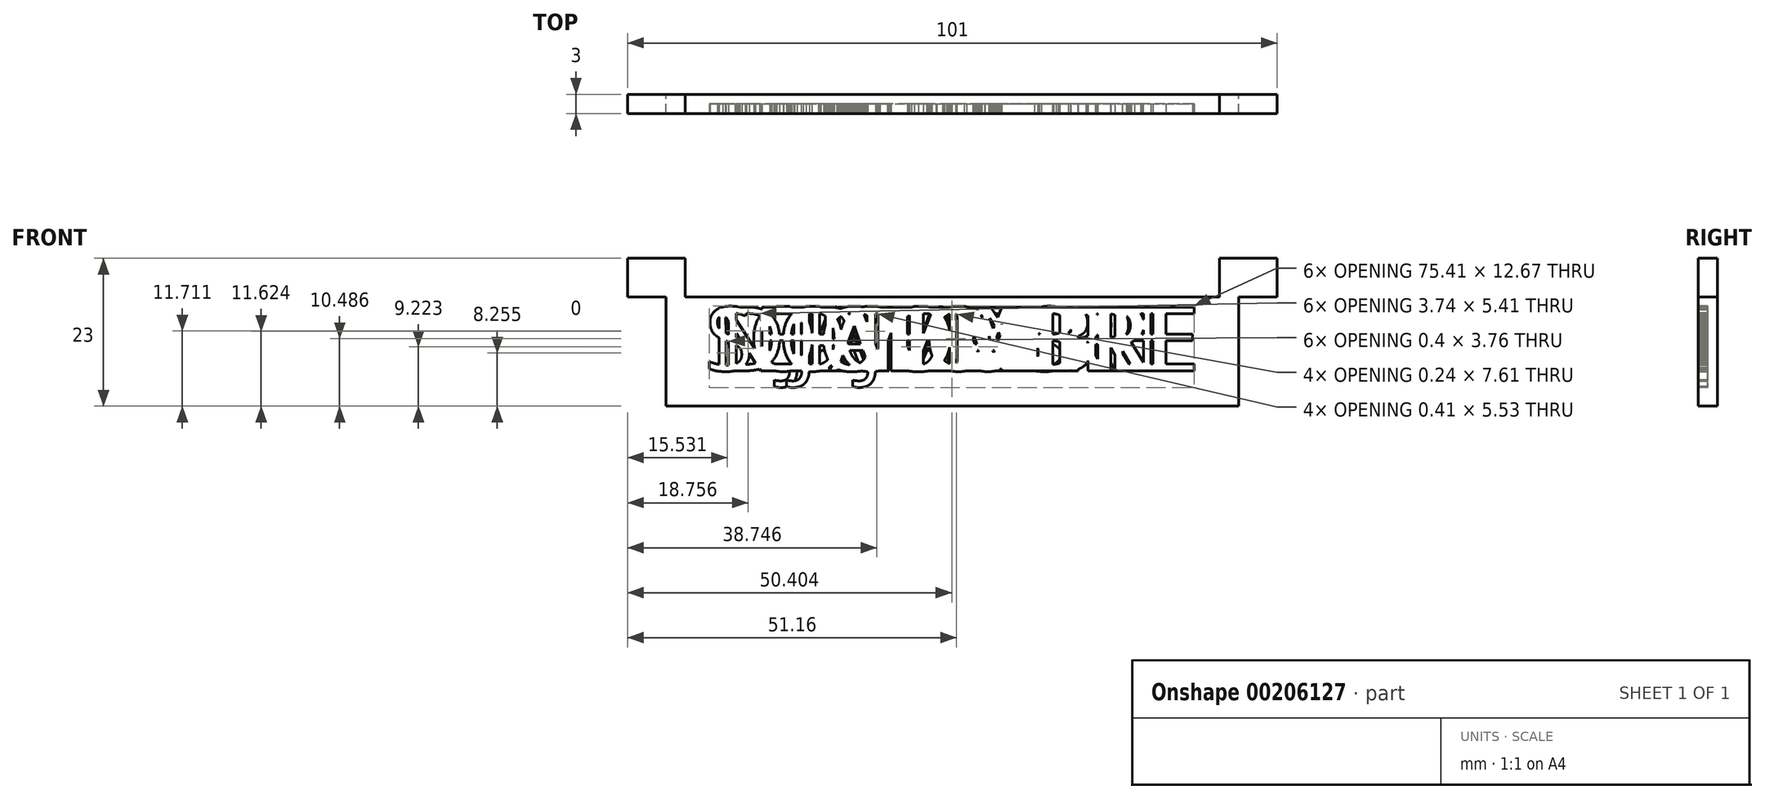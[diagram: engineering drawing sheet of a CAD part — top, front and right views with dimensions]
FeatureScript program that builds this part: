
annotation { "Feature Type Name" : "Feature", "Feature Type Description" : "" }
export const myFeature = defineFeature(function(context is Context, id is Id, definition is map)
    precondition{}
    {
        {
            var Q0;
            Q0=qCreatedBy(makeId("Front.planeOp"),FACE);
            var sketch = newSketch(context, id + "F0", { "sketchPlane" : qUnion([Q0])});
            skLineSegment(sketch, "E0.bottom", {"start": v(-51.5, 23) * mm, "end": v(-42.5, 23) * mm});
            skLineSegment(sketch, "E0.top", {"start": v(-45.5, 0) * mm, "end": v(43.5, 0) * mm});
            skLineSegment(sketch, "E0.left", {"start": v(-51.5, 23) * mm, "end": v(-51.5, 17) * mm});
            skLineSegment(sketch, "E0.right", {"start": v(49.5, 23) * mm, "end": v(49.5, 17) * mm});
            skLineSegment(sketch, "E1.top", {"start": v(-51.5, 17) * mm, "end": v(-45.5, 17) * mm});
            skLineSegment(sketch, "E1.right", {"start": v(-45.5, 0) * mm, "end": v(-45.5, 17) * mm});
            skLineSegment(sketch, "E2.bottom", {"start": v(-51.5, 23) * mm, "end": v(-42.5, 23) * mm, "construction": true});
            skLineSegment(sketch, "E2.top", {"start": v(-51.5, 17) * mm, "end": v(-42.5, 17) * mm, "construction": true});
            skLineSegment(sketch, "E2.left", {"start": v(-51.5, 23) * mm, "end": v(-51.5, 17) * mm, "construction": true});
            skLineSegment(sketch, "E2.right", {"start": v(-42.5, 23) * mm, "end": v(-42.5, 17) * mm, "construction": true});
            skLineSegment(sketch, "E3.top", {"start": v(-42.5, 17) * mm, "end": v(40.5, 17) * mm});
            skLineSegment(sketch, "E3.left", {"start": v(-42.5, 23) * mm, "end": v(-42.5, 17) * mm});
            skLineSegment(sketch, "E3.right", {"start": v(40.5, 23) * mm, "end": v(40.5, 17) * mm});
            skLineSegment(sketch, "E4.top", {"start": v(49.5, 17) * mm, "end": v(43.5, 17) * mm});
            skLineSegment(sketch, "E4.right", {"start": v(43.5, 0) * mm, "end": v(43.5, 17) * mm});
            skLineSegment(sketch, "E5.trimOffspring", {"start": v(40.5, 23) * mm, "end": v(49.5, 23) * mm});
            skSolve(sketch);
        }
        {
            var Q0;
            Q0=makeQuery(id+"F0.imprint","IMPRINT",FACE,{"disambiguationData":[TD([[makeQuery(id+"F0.imprint","IMPRINT",EDGE,{"derivedFrom":sQuery(id+"F0.wireOp",EDGE,"E0.bottom")}),-1.0]])]});
            extrude(context, id + "F1", {"entities" : qUnion([Q0]), "depth" : 3 * mm});
        }
        {
            var Q0;
            Q0=makeQuery(id+"F1.opExtrude","CAP_FACE",FACE,{"disambiguationData":[OSD([sQuery(id+"F0.wireOp",EDGE,"E0.bottom"),sQuery(id+"F0.wireOp",EDGE,"E0.top"),sQuery(id+"F0.wireOp",EDGE,"E0.left"),sQuery(id+"F0.wireOp",EDGE,"E0.right"),sQuery(id+"F0.wireOp",EDGE,"E1.top"),sQuery(id+"F0.wireOp",EDGE,"E1.right"),sQuery(id+"F0.wireOp",EDGE,"E3.top"),sQuery(id+"F0.wireOp",EDGE,"E3.left"),sQuery(id+"F0.wireOp",EDGE,"E3.right"),sQuery(id+"F0.wireOp",EDGE,"E4.top"),sQuery(id+"F0.wireOp",EDGE,"E4.right"),sQuery(id+"F0.wireOp",EDGE,"E5.trimOffspring")])],"isStart":false});
            var sketch = newSketch(context, id + "F2", { "sketchPlane" : qUnion([Q0])});
            skLineSegment(sketch, "E6.0", {"start": v(-45.5, 3.5) * mm, "end": v(-42, 3.5) * mm, "construction": true});
            skLineSegment(sketch, "E7.0", {"start": v(-42, 15.5) * mm, "end": v(40, 15.5) * mm, "construction": true});
            skLineSegment(sketch, "E8.0", {"start": v(-42, 0) * mm, "end": v(-42, 15.5) * mm, "construction": true});
            skText(sketch, "E9", { "text": "JANVIER", "fontName": "OpenSans-Regular.ttf"});
            skLineSegment(sketch, "E10.top", {"start": v(-45.5, 0) * mm, "end": v(-42, 0) * mm, "construction": true});
            skLineSegment(sketch, "E10.left", {"start": v(-45.5, 3.5) * mm, "end": v(-45.5, 0) * mm, "construction": true});
            skLineSegment(sketch, "E10.right", {"start": v(-42, 3.5) * mm, "end": v(-42, 0) * mm, "construction": true});
            skLineSegment(sketch, "E11.0", {"start": v(40, 0) * mm, "end": v(40, 17) * mm, "construction": true});
            skPoint(sketch, "E12.orphan", {"position": v(40, 15.5) * mm});
            skPoint(sketch, "E13.end.orphan", {"position": v(-1, 0) * mm});
            skLineSegment(sketch, "E14", {"start": v(-1, 17) * mm, "end": v(-1, 0) * mm, "construction": true});
            const initialGuessF2  = {"E9": [-0.02758, 0.0055, 1, 0, 0.01]};
            skSetInitialGuess(sketch, initialGuessF2);
            skSolve(sketch);
        }
        {
            var Q0;
            Q0=makeQuery(id+"F2.imprint","IMPRINT",FACE,{"disambiguationData":[TD([[makeQuery(id+"F2.imprint","IMPRINT",EDGE,{"derivedFrom":sQuery(id+"F2.wireOp",EDGE,"E9.sketch_text.stroke-0")}),-1.0]])]});
            var Q1;
            Q1=makeQuery(id+"F2.imprint","IMPRINT",FACE,{"disambiguationData":[TD([[makeQuery(id+"F2.imprint","IMPRINT",EDGE,{"derivedFrom":sQuery(id+"F2.wireOp",EDGE,"E9.sketch_text.stroke-10")}),-1.0]])]});
            var Q2;
            Q2=makeQuery(id+"F2.imprint","IMPRINT",FACE,{"disambiguationData":[TD([[makeQuery(id+"F2.imprint","IMPRINT",EDGE,{"derivedFrom":sQuery(id+"F2.wireOp",EDGE,"E9.sketch_text.stroke-23")}),-1.0]])]});
            var Q3;
            Q3=makeQuery(id+"F2.imprint","IMPRINT",FACE,{"disambiguationData":[TD([[makeQuery(id+"F2.imprint","IMPRINT",EDGE,{"derivedFrom":sQuery(id+"F2.wireOp",EDGE,"E9.sketch_text.stroke-38")}),-1.0]])]});
            var Q4;
            Q4=makeQuery(id+"F2.imprint","IMPRINT",FACE,{"disambiguationData":[TD([[makeQuery(id+"F2.imprint","IMPRINT",EDGE,{"derivedFrom":sQuery(id+"F2.wireOp",EDGE,"E9.sketch_text.stroke-52")}),-1.0]])]});
            var Q5;
            Q5=makeQuery(id+"F2.imprint","IMPRINT",FACE,{"disambiguationData":[TD([[makeQuery(id+"F2.imprint","IMPRINT",EDGE,{"derivedFrom":sQuery(id+"F2.wireOp",EDGE,"E9.sketch_text.stroke-65")}),-1.0]])]});
            var Q6;
            Q6=makeQuery(id+"F2.imprint","IMPRINT",FACE,{"disambiguationData":[TD([[makeQuery(id+"F2.imprint","IMPRINT",EDGE,{"derivedFrom":sQuery(id+"F2.wireOp",EDGE,"E9.sketch_text.stroke-47")}),-1.0]])]});
            extrude(context, id + "F3", {"entities" : qUnion([Q0, Q1, Q2, Q3, Q4, Q5, Q6]), "operationType" : NewBodyOperationType.REMOVE, "oppositeDirection" : true, "depth" : 1.5 * mm});
        }
        {
            var Q0;
            Q0=qSketchRegion(id+"F0",true);
            extrude(context, id + "F4", {"entities" : qUnion([Q0]), "depth" : 3 * mm});
        }
        {
            var Q0;
            Q0=makeQuery(id+"F4.opExtrude","CAP_FACE",FACE,{"disambiguationData":[OSD([sQuery(id+"F0.wireOp",EDGE,"E0.bottom"),sQuery(id+"F0.wireOp",EDGE,"E0.top"),sQuery(id+"F0.wireOp",EDGE,"E0.left"),sQuery(id+"F0.wireOp",EDGE,"E0.right"),sQuery(id+"F0.wireOp",EDGE,"E1.top"),sQuery(id+"F0.wireOp",EDGE,"E1.right"),sQuery(id+"F0.wireOp",EDGE,"E3.top"),sQuery(id+"F0.wireOp",EDGE,"E3.left"),sQuery(id+"F0.wireOp",EDGE,"E3.right"),sQuery(id+"F0.wireOp",EDGE,"E4.top"),sQuery(id+"F0.wireOp",EDGE,"E4.right"),sQuery(id+"F0.wireOp",EDGE,"E5.trimOffspring")])],"isStart":false});
            var sketch = newSketch(context, id + "F5", { "sketchPlane" : qUnion([Q0])});
            skText(sketch, "E15", { "text": "FEVRIER", "fontName": "OpenSans-Regular.ttf"});
            skPoint(sketch, "E16.orphan", {"position": v(36.68, 15.5) * mm});
            skPoint(sketch, "E17.end.orphan", {"position": v(-0.5, 0) * mm});
            skPoint(sketch, "E18.orphan", {"position": v(-38.68, 15.5) * mm});
            skLineSegment(sketch, "E19.0", {"start": v(-43.5, 15.5) * mm, "end": v(41.5, 15.5) * mm, "construction": true});
            skPoint(sketch, "E20.start.orphan", {"position": v(-1, 17) * mm});
            const initialGuessF5  = {"E15": [-0.0273, 0.0055, 1, 0, 0.01]};
            skSetInitialGuess(sketch, initialGuessF5);
            skSolve(sketch);
        }
        {
            var Q0;
            Q0=makeQuery(id+"F5.imprint","IMPRINT",FACE,{"disambiguationData":[TD([[makeQuery(id+"F5.imprint","IMPRINT",EDGE,{"derivedFrom":sQuery(id+"F5.wireOp",EDGE,"E15.sketch_text.stroke-0")}),-1.0]])]});
            var Q1;
            Q1=makeQuery(id+"F5.imprint","IMPRINT",FACE,{"disambiguationData":[TD([[makeQuery(id+"F5.imprint","IMPRINT",EDGE,{"derivedFrom":sQuery(id+"F5.wireOp",EDGE,"E15.sketch_text.stroke-10")}),-1.0]])]});
            var Q2;
            Q2=makeQuery(id+"F5.imprint","IMPRINT",FACE,{"disambiguationData":[TD([[makeQuery(id+"F5.imprint","IMPRINT",EDGE,{"derivedFrom":sQuery(id+"F5.wireOp",EDGE,"E15.sketch_text.stroke-22")}),-1.0]])]});
            var Q3;
            Q3=makeQuery(id+"F5.imprint","IMPRINT",FACE,{"disambiguationData":[TD([[makeQuery(id+"F5.imprint","IMPRINT",EDGE,{"derivedFrom":sQuery(id+"F5.wireOp",EDGE,"E15.sketch_text.stroke-47")}),-1.0]])]});
            var Q4;
            Q4=makeQuery(id+"F5.imprint","IMPRINT",FACE,{"disambiguationData":[TD([[makeQuery(id+"F5.imprint","IMPRINT",EDGE,{"derivedFrom":sQuery(id+"F5.wireOp",EDGE,"E15.sketch_text.stroke-65")}),-1.0]])]});
            var Q5;
            Q5=makeQuery(id+"F5.imprint","IMPRINT",FACE,{"disambiguationData":[TD([[makeQuery(id+"F5.imprint","IMPRINT",EDGE,{"derivedFrom":sQuery(id+"F5.wireOp",EDGE,"E15.sketch_text.stroke-79")}),-1.0]])]});
            var Q6;
            Q6=makeQuery(id+"F5.imprint","IMPRINT",FACE,{"disambiguationData":[TD([[makeQuery(id+"F5.imprint","IMPRINT",EDGE,{"derivedFrom":sQuery(id+"F5.wireOp",EDGE,"E15.sketch_text.stroke-49")}),-1.0]])]});
            var Q7;
            Q7=makeQuery(id+"F5.imprint","IMPRINT",FACE,{"disambiguationData":[TD([[makeQuery(id+"F5.imprint","IMPRINT",EDGE,{"derivedFrom":sQuery(id+"F5.wireOp",EDGE,"E15.sketch_text.stroke-53")}),-1.0]])]});
            extrude(context, id + "F6", {"entities" : qUnion([Q0, Q1, Q2, Q3, Q4, Q5, Q6, Q7]), "operationType" : NewBodyOperationType.REMOVE, "oppositeDirection" : true, "depth" : 1.5 * mm});
        }
        {
            var Q0;
            Q0=makeQuery(id+"F0.imprint","IMPRINT",FACE,{"disambiguationData":[TD([[makeQuery(id+"F0.imprint","IMPRINT",EDGE,{"derivedFrom":sQuery(id+"F0.wireOp",EDGE,"E0.bottom")}),-1.0]])]});
            extrude(context, id + "F7", {"entities" : qUnion([Q0]), "depth" : 3 * mm});
        }
        {
            var Q0;
            Q0=makeQuery(id+"F7.opExtrude","CAP_FACE",FACE,{"disambiguationData":[OSD([sQuery(id+"F0.wireOp",EDGE,"E0.bottom"),sQuery(id+"F0.wireOp",EDGE,"E0.top"),sQuery(id+"F0.wireOp",EDGE,"E0.left"),sQuery(id+"F0.wireOp",EDGE,"E0.right"),sQuery(id+"F0.wireOp",EDGE,"E1.top"),sQuery(id+"F0.wireOp",EDGE,"E1.right"),sQuery(id+"F0.wireOp",EDGE,"E3.top"),sQuery(id+"F0.wireOp",EDGE,"E3.left"),sQuery(id+"F0.wireOp",EDGE,"E3.right"),sQuery(id+"F0.wireOp",EDGE,"E4.top"),sQuery(id+"F0.wireOp",EDGE,"E4.right"),sQuery(id+"F0.wireOp",EDGE,"E5.trimOffspring")])],"isStart":false});
            var sketch = newSketch(context, id + "F8", { "sketchPlane" : qUnion([Q0])});
            skText(sketch, "E21", { "text": "MARS", "fontName": "OpenSans-Regular.ttf"});
            skPoint(sketch, "E22.orphan", {"position": v(29.28, 15.5) * mm});
            skPoint(sketch, "E23.end.orphan", {"position": v(0, -12.7) * mm});
            skPoint(sketch, "E24.orphan", {"position": v(-31.28, 15.5) * mm});
            skPoint(sketch, "E25.start.orphan", {"position": v(0, 4.3) * mm});
            skLineSegment(sketch, "E26.0", {"start": v(-43.5, 15.5) * mm, "end": v(41.5, 15.5) * mm, "construction": true});
            const initialGuessF8  = {"E21": [-0.01989, 0.0055, 1, 0, 0.01]};
            skSetInitialGuess(sketch, initialGuessF8);
            skSolve(sketch);
        }
        {
            var Q0;
            Q0=makeQuery(id+"F8.imprint","IMPRINT",FACE,{"disambiguationData":[TD([[makeQuery(id+"F8.imprint","IMPRINT",EDGE,{"derivedFrom":sQuery(id+"F8.wireOp",EDGE,"E21.sketch_text.stroke-0")}),-1.0]])]});
            var Q1;
            Q1=makeQuery(id+"F8.imprint","IMPRINT",FACE,{"disambiguationData":[TD([[makeQuery(id+"F8.imprint","IMPRINT",EDGE,{"derivedFrom":sQuery(id+"F8.wireOp",EDGE,"E21.sketch_text.stroke-18")}),-1.0]])]});
            var Q2;
            Q2=makeQuery(id+"F8.imprint","IMPRINT",FACE,{"disambiguationData":[TD([[makeQuery(id+"F8.imprint","IMPRINT",EDGE,{"derivedFrom":sQuery(id+"F8.wireOp",EDGE,"E21.sketch_text.stroke-31")}),-1.0]])]});
            var Q3;
            Q3=makeQuery(id+"F8.imprint","IMPRINT",FACE,{"disambiguationData":[TD([[makeQuery(id+"F8.imprint","IMPRINT",EDGE,{"derivedFrom":sQuery(id+"F8.wireOp",EDGE,"E21.sketch_text.stroke-49")}),-1.0]])]});
            var Q4;
            Q4=makeQuery(id+"F8.imprint","IMPRINT",FACE,{"disambiguationData":[TD([[makeQuery(id+"F8.imprint","IMPRINT",EDGE,{"derivedFrom":sQuery(id+"F8.wireOp",EDGE,"E21.sketch_text.stroke-64")}),-1.0]])]});
            extrude(context, id + "F9", {"entities" : qUnion([Q0, Q1, Q2, Q3, Q4]), "operationType" : NewBodyOperationType.REMOVE, "oppositeDirection" : true, "depth" : 1.5 * mm});
        }
        {
            var Q0;
            Q0=makeQuery(id+"F0.imprint","IMPRINT",FACE,{"disambiguationData":[TD([[makeQuery(id+"F0.imprint","IMPRINT",EDGE,{"derivedFrom":sQuery(id+"F0.wireOp",EDGE,"E0.bottom")}),-1.0]])]});
            extrude(context, id + "F10", {"entities" : qUnion([Q0]), "depth" : 3 * mm});
        }
        {
            var Q0;
            Q0=makeQuery(id+"F10.opExtrude","CAP_FACE",FACE,{"disambiguationData":[OSD([sQuery(id+"F0.wireOp",EDGE,"E0.bottom"),sQuery(id+"F0.wireOp",EDGE,"E0.top"),sQuery(id+"F0.wireOp",EDGE,"E0.left"),sQuery(id+"F0.wireOp",EDGE,"E0.right"),sQuery(id+"F0.wireOp",EDGE,"E1.top"),sQuery(id+"F0.wireOp",EDGE,"E1.right"),sQuery(id+"F0.wireOp",EDGE,"E3.top"),sQuery(id+"F0.wireOp",EDGE,"E3.left"),sQuery(id+"F0.wireOp",EDGE,"E3.right"),sQuery(id+"F0.wireOp",EDGE,"E4.top"),sQuery(id+"F0.wireOp",EDGE,"E4.right"),sQuery(id+"F0.wireOp",EDGE,"E5.trimOffspring")])],"isStart":false});
            var sketch = newSketch(context, id + "F11", { "sketchPlane" : qUnion([Q0])});
            skText(sketch, "E27", { "text": "AVRIL", "fontName": "OpenSans-Regular.ttf"});
            skPoint(sketch, "E28.orphan", {"position": v(29.04, 15.5) * mm});
            skPoint(sketch, "E29.end.orphan", {"position": v(0.3, -20.32) * mm});
            skPoint(sketch, "E30.orphan", {"position": v(-31.04, 15.5) * mm});
            skPoint(sketch, "E31.start.orphan", {"position": v(0.3, -3.32) * mm});
            skLineSegment(sketch, "E32.0", {"start": v(-43.5, 15.5) * mm, "end": v(41.5, 15.5) * mm});
            const initialGuessF11  = {"E27": [-0.01965, 0.0055, 1, 0, 0.01]};
            skSetInitialGuess(sketch, initialGuessF11);
            skSolve(sketch);
        }
        {
            var Q0;
            Q0=makeQuery(id+"F11.imprint","IMPRINT",FACE,{"disambiguationData":[TD([[makeQuery(id+"F11.imprint","IMPRINT",EDGE,{"derivedFrom":sQuery(id+"F11.wireOp",EDGE,"E27.sketch_text.stroke-0")}),-1.0]])]});
            var Q1;
            Q1=makeQuery(id+"F11.imprint","IMPRINT",FACE,{"disambiguationData":[TD([[makeQuery(id+"F11.imprint","IMPRINT",EDGE,{"derivedFrom":sQuery(id+"F11.wireOp",EDGE,"E27.sketch_text.stroke-13")}),-1.0]])]});
            var Q2;
            Q2=makeQuery(id+"F11.imprint","IMPRINT",FACE,{"disambiguationData":[TD([[makeQuery(id+"F11.imprint","IMPRINT",EDGE,{"derivedFrom":sQuery(id+"F11.wireOp",EDGE,"E27.sketch_text.stroke-28")}),-1.0]])]});
            var Q3;
            Q3=makeQuery(id+"F11.imprint","IMPRINT",FACE,{"disambiguationData":[TD([[makeQuery(id+"F11.imprint","IMPRINT",EDGE,{"derivedFrom":sQuery(id+"F11.wireOp",EDGE,"E27.sketch_text.stroke-46")}),-1.0]])]});
            var Q4;
            Q4=makeQuery(id+"F11.imprint","IMPRINT",FACE,{"disambiguationData":[TD([[makeQuery(id+"F11.imprint","IMPRINT",EDGE,{"derivedFrom":sQuery(id+"F11.wireOp",EDGE,"E27.sketch_text.stroke-40")}),-1.0]])]});
            extrude(context, id + "F12", {"entities" : qUnion([Q0, Q1, Q2, Q3, Q4]), "operationType" : NewBodyOperationType.REMOVE, "oppositeDirection" : true, "depth" : 1.5 * mm});
        }
        {
            var Q0;
            Q0=makeQuery(id+"F0.imprint","IMPRINT",FACE,{"disambiguationData":[TD([[makeQuery(id+"F0.imprint","IMPRINT",EDGE,{"derivedFrom":sQuery(id+"F0.wireOp",EDGE,"E0.bottom")}),-1.0]])]});
            extrude(context, id + "F13", {"entities" : qUnion([Q0]), "depth" : 3 * mm});
        }
        {
            var Q0;
            Q0=makeQuery(id+"F13.opExtrude","CAP_FACE",FACE,{"disambiguationData":[OSD([sQuery(id+"F0.wireOp",EDGE,"E0.bottom"),sQuery(id+"F0.wireOp",EDGE,"E0.top"),sQuery(id+"F0.wireOp",EDGE,"E0.left"),sQuery(id+"F0.wireOp",EDGE,"E0.right"),sQuery(id+"F0.wireOp",EDGE,"E1.top"),sQuery(id+"F0.wireOp",EDGE,"E1.right"),sQuery(id+"F0.wireOp",EDGE,"E3.top"),sQuery(id+"F0.wireOp",EDGE,"E3.left"),sQuery(id+"F0.wireOp",EDGE,"E3.right"),sQuery(id+"F0.wireOp",EDGE,"E4.top"),sQuery(id+"F0.wireOp",EDGE,"E4.right"),sQuery(id+"F0.wireOp",EDGE,"E5.trimOffspring")])],"isStart":false});
            var sketch = newSketch(context, id + "F14", { "sketchPlane" : qUnion([Q0])});
            skText(sketch, "E33", { "text": "MAI", "fontName": "OpenSans-Regular.ttf"});
            skPoint(sketch, "E34.orphan", {"position": v(22.76, 15.5) * mm});
            skPoint(sketch, "E35.end.orphan", {"position": v(0.48, -24.9) * mm});
            skPoint(sketch, "E36.orphan", {"position": v(-24.76, 15.5) * mm});
            skPoint(sketch, "E37.start.orphan", {"position": v(0.48, -7.9) * mm});
            skLineSegment(sketch, "E38.0", {"start": v(-37.67, 15.5) * mm, "end": v(35.67, 15.5) * mm});
            skLineSegment(sketch, "E39.0", {"start": v(-43.5, 15.5) * mm, "end": v(41.5, 15.5) * mm});
            const initialGuessF14  = {"E33": [-0.01337, 0.0055, 1, 0, 0.01]};
            skSetInitialGuess(sketch, initialGuessF14);
            skSolve(sketch);
        }
        {
            var Q0;
            Q0=makeQuery(id+"F0.imprint","IMPRINT",FACE,{"disambiguationData":[TD([[makeQuery(id+"F0.imprint","IMPRINT",EDGE,{"derivedFrom":sQuery(id+"F0.wireOp",EDGE,"E0.bottom")}),-1.0]])]});
            extrude(context, id + "F15", {"entities" : qUnion([Q0]), "depth" : 3 * mm});
        }
        {
            var Q0;
            Q0=makeQuery(id+"F15.opExtrude","CAP_FACE",FACE,{"disambiguationData":[OSD([sQuery(id+"F0.wireOp",EDGE,"E0.bottom"),sQuery(id+"F0.wireOp",EDGE,"E0.top"),sQuery(id+"F0.wireOp",EDGE,"E0.left"),sQuery(id+"F0.wireOp",EDGE,"E0.right"),sQuery(id+"F0.wireOp",EDGE,"E1.top"),sQuery(id+"F0.wireOp",EDGE,"E1.right"),sQuery(id+"F0.wireOp",EDGE,"E3.top"),sQuery(id+"F0.wireOp",EDGE,"E3.left"),sQuery(id+"F0.wireOp",EDGE,"E3.right"),sQuery(id+"F0.wireOp",EDGE,"E4.top"),sQuery(id+"F0.wireOp",EDGE,"E4.right"),sQuery(id+"F0.wireOp",EDGE,"E5.trimOffspring")])],"isStart":false});
            var sketch = newSketch(context, id + "F16", { "sketchPlane" : qUnion([Q0])});
            skText(sketch, "E40", { "text": "JUIN", "fontName": "OpenSans-Regular.ttf"});
            skPoint(sketch, "E41.orphan", {"position": v(24.78, 15.5) * mm});
            skPoint(sketch, "E42.end.orphan", {"position": v(0.65, -29.76) * mm});
            skPoint(sketch, "E43.orphan", {"position": v(-26.78, 15.5) * mm});
            skPoint(sketch, "E44.start.orphan", {"position": v(0.65, -12.76) * mm});
            skLineSegment(sketch, "E45.0", {"start": v(-39.7, 15.5) * mm, "end": v(37.7, 15.5) * mm});
            skLineSegment(sketch, "E46.0", {"start": v(-43.39, 15.5) * mm, "end": v(41.39, 15.5) * mm});
            skLineSegment(sketch, "E47.0", {"start": v(-43.5, 15.5) * mm, "end": v(41.5, 15.5) * mm});
            const initialGuessF16  = {"E40": [-0.0154, 0.0055, 1, 0, 0.01]};
            skSetInitialGuess(sketch, initialGuessF16);
            skSolve(sketch);
        }
        {
            var Q0;
            Q0=makeQuery(id+"F0.imprint","IMPRINT",FACE,{"disambiguationData":[TD([[makeQuery(id+"F0.imprint","IMPRINT",EDGE,{"derivedFrom":sQuery(id+"F0.wireOp",EDGE,"E0.bottom")}),-1.0]])]});
            extrude(context, id + "F17", {"entities" : qUnion([Q0]), "depth" : 3 * mm});
        }
        {
            var Q0;
            Q0=makeQuery(id+"F17.opExtrude","CAP_FACE",FACE,{"disambiguationData":[OSD([sQuery(id+"F0.wireOp",EDGE,"E0.bottom"),sQuery(id+"F0.wireOp",EDGE,"E0.top"),sQuery(id+"F0.wireOp",EDGE,"E0.left"),sQuery(id+"F0.wireOp",EDGE,"E0.right"),sQuery(id+"F0.wireOp",EDGE,"E1.top"),sQuery(id+"F0.wireOp",EDGE,"E1.right"),sQuery(id+"F0.wireOp",EDGE,"E3.top"),sQuery(id+"F0.wireOp",EDGE,"E3.left"),sQuery(id+"F0.wireOp",EDGE,"E3.right"),sQuery(id+"F0.wireOp",EDGE,"E4.top"),sQuery(id+"F0.wireOp",EDGE,"E4.right"),sQuery(id+"F0.wireOp",EDGE,"E5.trimOffspring")])],"isStart":false});
            var sketch = newSketch(context, id + "F18", { "sketchPlane" : qUnion([Q0])});
            skText(sketch, "E48", { "text": "JUILLET", "fontName": "OpenSans-Regular.ttf"});
            skPoint(sketch, "E49.orphan", {"position": v(35.08, 15.5) * mm});
            skPoint(sketch, "E50.end.orphan", {"position": v(0.82, -34.76) * mm});
            skPoint(sketch, "E51.orphan", {"position": v(-37.08, 15.5) * mm});
            skPoint(sketch, "E52.start.orphan", {"position": v(0.82, -17.76) * mm});
            skLineSegment(sketch, "E53.0", {"start": v(-49.99, 15.5) * mm, "end": v(47.99, 15.5) * mm});
            skLineSegment(sketch, "E54.0", {"start": v(-53.68, 15.5) * mm, "end": v(51.68, 15.5) * mm});
            skLineSegment(sketch, "E55.0", {"start": v(-52.1, 15.5) * mm, "end": v(50.1, 15.5) * mm});
            skLineSegment(sketch, "E56.0", {"start": v(-43.5, 15.5) * mm, "end": v(41.5, 15.5) * mm});
            const initialGuessF18  = {"E48": [-0.02569, 0.0055, 1, 0, 0.01]};
            skSetInitialGuess(sketch, initialGuessF18);
            skSolve(sketch);
        }
        {
            var Q0;
            Q0=makeQuery(id+"F0.imprint","IMPRINT",FACE,{"disambiguationData":[TD([[makeQuery(id+"F0.imprint","IMPRINT",EDGE,{"derivedFrom":sQuery(id+"F0.wireOp",EDGE,"E0.bottom")}),-1.0]])]});
            extrude(context, id + "F19", {"entities" : qUnion([Q0]), "depth" : 3 * mm});
        }
        {
            var Q0;
            Q0=makeQuery(id+"F19.opExtrude","CAP_FACE",FACE,{"disambiguationData":[OSD([sQuery(id+"F0.wireOp",EDGE,"E0.bottom"),sQuery(id+"F0.wireOp",EDGE,"E0.top"),sQuery(id+"F0.wireOp",EDGE,"E0.left"),sQuery(id+"F0.wireOp",EDGE,"E0.right"),sQuery(id+"F0.wireOp",EDGE,"E1.top"),sQuery(id+"F0.wireOp",EDGE,"E1.right"),sQuery(id+"F0.wireOp",EDGE,"E3.top"),sQuery(id+"F0.wireOp",EDGE,"E3.left"),sQuery(id+"F0.wireOp",EDGE,"E3.right"),sQuery(id+"F0.wireOp",EDGE,"E4.top"),sQuery(id+"F0.wireOp",EDGE,"E4.right"),sQuery(id+"F0.wireOp",EDGE,"E5.trimOffspring")])],"isStart":false});
            var sketch = newSketch(context, id + "F20", { "sketchPlane" : qUnion([Q0])});
            skText(sketch, "E57", { "text": "AOUT", "fontName": "OpenSans-Regular.ttf"});
            skPoint(sketch, "E58.orphan", {"position": v(29.48, 15.5) * mm});
            skPoint(sketch, "E59.end.orphan", {"position": v(1, -39.82) * mm});
            skPoint(sketch, "E60.orphan", {"position": v(-31.48, 15.5) * mm});
            skPoint(sketch, "E61.start.orphan", {"position": v(1, -22.82) * mm});
            skLineSegment(sketch, "E62.0", {"start": v(-44.39, 15.5) * mm, "end": v(42.39, 15.5) * mm});
            skLineSegment(sketch, "E63.0", {"start": v(-48.08, 15.5) * mm, "end": v(46.08, 15.5) * mm});
            skLineSegment(sketch, "E64.0", {"start": v(-46.5, 15.5) * mm, "end": v(44.5, 15.5) * mm});
            skLineSegment(sketch, "E65.0", {"start": v(-47.69, 15.5) * mm, "end": v(45.69, 15.5) * mm});
            skLineSegment(sketch, "E66.0", {"start": v(-43.5, 15.5) * mm, "end": v(41.5, 15.5) * mm});
            const initialGuessF20  = {"E57": [-0.02009, 0.0055, 1, 0, 0.01]};
            skSetInitialGuess(sketch, initialGuessF20);
            skSolve(sketch);
        }
        {
            var Q0;
            Q0=makeQuery(id+"F0.imprint","IMPRINT",FACE,{"disambiguationData":[TD([[makeQuery(id+"F0.imprint","IMPRINT",EDGE,{"derivedFrom":sQuery(id+"F0.wireOp",EDGE,"E0.bottom")}),-1.0]])]});
            extrude(context, id + "F21", {"entities" : qUnion([Q0]), "depth" : 3 * mm});
        }
        {
            var Q0;
            Q0=makeQuery(id+"F21.opExtrude","CAP_FACE",FACE,{"disambiguationData":[OSD([sQuery(id+"F0.wireOp",EDGE,"E0.bottom"),sQuery(id+"F0.wireOp",EDGE,"E0.top"),sQuery(id+"F0.wireOp",EDGE,"E0.left"),sQuery(id+"F0.wireOp",EDGE,"E0.right"),sQuery(id+"F0.wireOp",EDGE,"E1.top"),sQuery(id+"F0.wireOp",EDGE,"E1.right"),sQuery(id+"F0.wireOp",EDGE,"E3.top"),sQuery(id+"F0.wireOp",EDGE,"E3.left"),sQuery(id+"F0.wireOp",EDGE,"E3.right"),sQuery(id+"F0.wireOp",EDGE,"E4.top"),sQuery(id+"F0.wireOp",EDGE,"E4.right"),sQuery(id+"F0.wireOp",EDGE,"E5.trimOffspring")])],"isStart":false});
            var sketch = newSketch(context, id + "F22", { "sketchPlane" : qUnion([Q0])});
            skText(sketch, "E67", { "text": "SEPTEMBRE", "fontName": "OpenSans-Regular.ttf"});
            skPoint(sketch, "E68.orphan", {"position": v(48.9, 15.5) * mm});
            skPoint(sketch, "E69.end.orphan", {"position": v(1.16, -44.91) * mm});
            skPoint(sketch, "E70.orphan", {"position": v(-50.9, 15.5) * mm});
            skPoint(sketch, "E71.start.orphan", {"position": v(1.16, -27.91) * mm});
            const initialGuessF22  = {"E67": [-0.03952, 0.0055, 1, 0, 0.01]};
            skSetInitialGuess(sketch, initialGuessF22);
            skSolve(sketch);
        }
        {
            var Q0;
            Q0=makeQuery(id+"F0.imprint","IMPRINT",FACE,{"disambiguationData":[TD([[makeQuery(id+"F0.imprint","IMPRINT",EDGE,{"derivedFrom":sQuery(id+"F0.wireOp",EDGE,"E0.bottom")}),-1.0]])]});
            extrude(context, id + "F23", {"entities" : qUnion([Q0]), "depth" : 3 * mm});
        }
        {
            var Q0;
            Q0=makeQuery(id+"F23.opExtrude","CAP_FACE",FACE,{"disambiguationData":[OSD([sQuery(id+"F0.wireOp",EDGE,"E0.bottom"),sQuery(id+"F0.wireOp",EDGE,"E0.top"),sQuery(id+"F0.wireOp",EDGE,"E0.left"),sQuery(id+"F0.wireOp",EDGE,"E0.right"),sQuery(id+"F0.wireOp",EDGE,"E1.top"),sQuery(id+"F0.wireOp",EDGE,"E1.right"),sQuery(id+"F0.wireOp",EDGE,"E3.top"),sQuery(id+"F0.wireOp",EDGE,"E3.left"),sQuery(id+"F0.wireOp",EDGE,"E3.right"),sQuery(id+"F0.wireOp",EDGE,"E4.top"),sQuery(id+"F0.wireOp",EDGE,"E4.right"),sQuery(id+"F0.wireOp",EDGE,"E5.trimOffspring")])],"isStart":false});
            var sketch = newSketch(context, id + "F24", { "sketchPlane" : qUnion([Q0])});
            skText(sketch, "E72", { "text": "OCTOBRE", "fontName": "OpenSans-Regular.ttf"});
            skPoint(sketch, "E73.orphan", {"position": v(42.12, 15.5) * mm});
            skPoint(sketch, "E74.end.orphan", {"position": v(1.08, -34.46) * mm});
            skPoint(sketch, "E75.orphan", {"position": v(-44.12, 15.5) * mm});
            skPoint(sketch, "E76.start.orphan", {"position": v(1.08, -17.46) * mm});
            skLineSegment(sketch, "E77.0", {"start": v(-42.5, 15.5) * mm, "end": v(40.5, 15.5) * mm});
            const initialGuessF24  = {"E72": [-0.03273, 0.0055, 1, 0, 0.01]};
            skSetInitialGuess(sketch, initialGuessF24);
            skSolve(sketch);
        }
        {
            var Q0;
            Q0=makeQuery(id+"F0.imprint","IMPRINT",FACE,{"disambiguationData":[TD([[makeQuery(id+"F0.imprint","IMPRINT",EDGE,{"derivedFrom":sQuery(id+"F0.wireOp",EDGE,"E0.bottom")}),-1.0]])]});
            extrude(context, id + "F25", {"entities" : qUnion([Q0]), "depth" : 3 * mm});
        }
        {
            var Q0;
            Q0=makeQuery(id+"F25.opExtrude","CAP_FACE",FACE,{"disambiguationData":[OSD([sQuery(id+"F0.wireOp",EDGE,"E0.bottom"),sQuery(id+"F0.wireOp",EDGE,"E0.top"),sQuery(id+"F0.wireOp",EDGE,"E0.left"),sQuery(id+"F0.wireOp",EDGE,"E0.right"),sQuery(id+"F0.wireOp",EDGE,"E1.top"),sQuery(id+"F0.wireOp",EDGE,"E1.right"),sQuery(id+"F0.wireOp",EDGE,"E3.top"),sQuery(id+"F0.wireOp",EDGE,"E3.left"),sQuery(id+"F0.wireOp",EDGE,"E3.right"),sQuery(id+"F0.wireOp",EDGE,"E4.top"),sQuery(id+"F0.wireOp",EDGE,"E4.right"),sQuery(id+"F0.wireOp",EDGE,"E5.trimOffspring")])],"isStart":false});
            var sketch = newSketch(context, id + "F26", { "sketchPlane" : qUnion([Q0])});
            skText(sketch, "E78", { "text": "NOVEMBRE", "fontName": "OpenSans-Regular.ttf"});
            skPoint(sketch, "E79.orphan", {"position": v(47.99, 15.5) * mm});
            skPoint(sketch, "E80.end.orphan", {"position": v(1.08, -34.46) * mm});
            skPoint(sketch, "E81.orphan", {"position": v(-49.99, 15.5) * mm});
            skPoint(sketch, "E82.start.orphan", {"position": v(1.08, -17.46) * mm});
            skLineSegment(sketch, "E83.0", {"start": v(-42.5, 15.5) * mm, "end": v(40.5, 15.5) * mm});
            const initialGuessF26  = {"E78": [-0.0386, 0.0055, 1, 0, 0.01]};
            skSetInitialGuess(sketch, initialGuessF26);
            skSolve(sketch);
        }
        {
            var Q0;
            Q0=makeQuery(id+"F0.imprint","IMPRINT",FACE,{"disambiguationData":[TD([[makeQuery(id+"F0.imprint","IMPRINT",EDGE,{"derivedFrom":sQuery(id+"F0.wireOp",EDGE,"E0.bottom")}),-1.0]])]});
            extrude(context, id + "F27", {"entities" : qUnion([Q0]), "depth" : 3 * mm});
        }
        {
            var Q0;
            Q0=makeQuery(id+"F27.opExtrude","CAP_FACE",FACE,{"disambiguationData":[OSD([sQuery(id+"F0.wireOp",EDGE,"E0.bottom"),sQuery(id+"F0.wireOp",EDGE,"E0.top"),sQuery(id+"F0.wireOp",EDGE,"E0.left"),sQuery(id+"F0.wireOp",EDGE,"E0.right"),sQuery(id+"F0.wireOp",EDGE,"E1.top"),sQuery(id+"F0.wireOp",EDGE,"E1.right"),sQuery(id+"F0.wireOp",EDGE,"E3.top"),sQuery(id+"F0.wireOp",EDGE,"E3.left"),sQuery(id+"F0.wireOp",EDGE,"E3.right"),sQuery(id+"F0.wireOp",EDGE,"E4.top"),sQuery(id+"F0.wireOp",EDGE,"E4.right"),sQuery(id+"F0.wireOp",EDGE,"E5.trimOffspring")])],"isStart":false});
            var sketch = newSketch(context, id + "F28", { "sketchPlane" : qUnion([Q0])});
            skText(sketch, "E84", { "text": "DECEMBRE", "fontName": "OpenSans-Regular.ttf"});
            skPoint(sketch, "E85.orphan", {"position": v(46.52, 15.5) * mm});
            skPoint(sketch, "E86.end.orphan", {"position": v(1.08, -34.46) * mm});
            skPoint(sketch, "E87.orphan", {"position": v(-48.52, 15.5) * mm});
            skPoint(sketch, "E88.start.orphan", {"position": v(1.08, -17.46) * mm});
            skLineSegment(sketch, "E89.0", {"start": v(-42.5, 15.5) * mm, "end": v(40.5, 15.5) * mm});
            const initialGuessF28  = {"E84": [-0.03713, 0.0055, 1, 0, 0.01]};
            skSetInitialGuess(sketch, initialGuessF28);
            skSolve(sketch);
        }
        {
            var Q0;
            Q0=makeQuery(id+"F28.imprint","IMPRINT",FACE,{"disambiguationData":[TD([[makeQuery(id+"F28.imprint","IMPRINT",EDGE,{"derivedFrom":sQuery(id+"F28.wireOp",EDGE,"E84.sketch_text.stroke-0")}),-1.0]])]});
            var Q1;
            Q1=makeQuery(id+"F28.imprint","IMPRINT",FACE,{"disambiguationData":[TD([[makeQuery(id+"F28.imprint","IMPRINT",EDGE,{"derivedFrom":sQuery(id+"F28.wireOp",EDGE,"E84.sketch_text.stroke-14")}),-1.0]])]});
            var Q2;
            Q2=makeQuery(id+"F28.imprint","IMPRINT",FACE,{"disambiguationData":[TD([[makeQuery(id+"F28.imprint","IMPRINT",EDGE,{"derivedFrom":sQuery(id+"F28.wireOp",EDGE,"E84.sketch_text.stroke-26")}),-1.0]])]});
            var Q3;
            Q3=makeQuery(id+"F28.imprint","IMPRINT",FACE,{"disambiguationData":[TD([[makeQuery(id+"F28.imprint","IMPRINT",EDGE,{"derivedFrom":sQuery(id+"F28.wireOp",EDGE,"E84.sketch_text.stroke-41")}),-1.0]])]});
            var Q4;
            Q4=makeQuery(id+"F28.imprint","IMPRINT",FACE,{"disambiguationData":[TD([[makeQuery(id+"F28.imprint","IMPRINT",EDGE,{"derivedFrom":sQuery(id+"F28.wireOp",EDGE,"E84.sketch_text.stroke-53")}),-1.0]])]});
            var Q5;
            Q5=makeQuery(id+"F28.imprint","IMPRINT",FACE,{"disambiguationData":[TD([[makeQuery(id+"F28.imprint","IMPRINT",EDGE,{"derivedFrom":sQuery(id+"F28.wireOp",EDGE,"E84.sketch_text.stroke-71")}),-1.0]])]});
            var Q6;
            Q6=makeQuery(id+"F28.imprint","IMPRINT",FACE,{"disambiguationData":[TD([[makeQuery(id+"F28.imprint","IMPRINT",EDGE,{"derivedFrom":sQuery(id+"F28.wireOp",EDGE,"E84.sketch_text.stroke-96")}),-1.0]])]});
            var Q7;
            Q7=makeQuery(id+"F28.imprint","IMPRINT",FACE,{"disambiguationData":[TD([[makeQuery(id+"F28.imprint","IMPRINT",EDGE,{"derivedFrom":sQuery(id+"F28.wireOp",EDGE,"E84.sketch_text.stroke-108")}),-1.0]])]});
            var Q8;
            Q8=makeQuery(id+"F28.imprint","IMPRINT",FACE,{"disambiguationData":[TD([[makeQuery(id+"F28.imprint","IMPRINT",EDGE,{"derivedFrom":sQuery(id+"F28.wireOp",EDGE,"E84.sketch_text.stroke-114")}),-1.0]])]});
            extrude(context, id + "F29", {"entities" : qUnion([Q0, Q1, Q2, Q3, Q4, Q5, Q6, Q7, Q8]), "operationType" : NewBodyOperationType.REMOVE, "oppositeDirection" : true, "depth" : 1.5 * mm});
        }
        {
            var Q0;
            Q0=makeQuery(id+"F26.imprint","IMPRINT",FACE,{"disambiguationData":[TD([[makeQuery(id+"F26.imprint","IMPRINT",EDGE,{"derivedFrom":sQuery(id+"F26.wireOp",EDGE,"E78.sketch_text.stroke-0")}),-1.0]])]});
            var Q1;
            Q1=makeQuery(id+"F26.imprint","IMPRINT",FACE,{"disambiguationData":[TD([[makeQuery(id+"F26.imprint","IMPRINT",EDGE,{"derivedFrom":sQuery(id+"F26.wireOp",EDGE,"E78.sketch_text.stroke-15")}),-1.0]])]});
            var Q2;
            Q2=makeQuery(id+"F26.imprint","IMPRINT",FACE,{"disambiguationData":[TD([[makeQuery(id+"F26.imprint","IMPRINT",EDGE,{"derivedFrom":sQuery(id+"F26.wireOp",EDGE,"E78.sketch_text.stroke-31")}),-1.0]])]});
            var Q3;
            Q3=makeQuery(id+"F26.imprint","IMPRINT",FACE,{"disambiguationData":[TD([[makeQuery(id+"F26.imprint","IMPRINT",EDGE,{"derivedFrom":sQuery(id+"F26.wireOp",EDGE,"E78.sketch_text.stroke-40")}),-1.0]])]});
            var Q4;
            Q4=makeQuery(id+"F26.imprint","IMPRINT",FACE,{"disambiguationData":[TD([[makeQuery(id+"F26.imprint","IMPRINT",EDGE,{"derivedFrom":sQuery(id+"F26.wireOp",EDGE,"E78.sketch_text.stroke-52")}),-1.0]])]});
            var Q5;
            Q5=makeQuery(id+"F26.imprint","IMPRINT",FACE,{"disambiguationData":[TD([[makeQuery(id+"F26.imprint","IMPRINT",EDGE,{"derivedFrom":sQuery(id+"F26.wireOp",EDGE,"E78.sketch_text.stroke-70")}),-1.0]])]});
            var Q6;
            Q6=makeQuery(id+"F26.imprint","IMPRINT",FACE,{"disambiguationData":[TD([[makeQuery(id+"F26.imprint","IMPRINT",EDGE,{"derivedFrom":sQuery(id+"F26.wireOp",EDGE,"E78.sketch_text.stroke-95")}),-1.0]])]});
            var Q7;
            Q7=makeQuery(id+"F26.imprint","IMPRINT",FACE,{"disambiguationData":[TD([[makeQuery(id+"F26.imprint","IMPRINT",EDGE,{"derivedFrom":sQuery(id+"F26.wireOp",EDGE,"E78.sketch_text.stroke-107")}),-1.0]])]});
            var Q8;
            Q8=makeQuery(id+"F26.imprint","IMPRINT",FACE,{"disambiguationData":[TD([[makeQuery(id+"F26.imprint","IMPRINT",EDGE,{"derivedFrom":sQuery(id+"F26.wireOp",EDGE,"E78.sketch_text.stroke-113")}),-1.0]])]});
            extrude(context, id + "F30", {"entities" : qUnion([Q0, Q1, Q2, Q3, Q4, Q5, Q6, Q7, Q8]), "operationType" : NewBodyOperationType.REMOVE, "oppositeDirection" : true, "depth" : 1.5 * mm});
        }
        {
            var Q0;
            Q0=makeQuery(id+"F24.imprint","IMPRINT",FACE,{"disambiguationData":[TD([[makeQuery(id+"F24.imprint","IMPRINT",EDGE,{"derivedFrom":sQuery(id+"F24.wireOp",EDGE,"E72.sketch_text.stroke-0")}),-1.0]])]});
            var Q1;
            Q1=makeQuery(id+"F24.imprint","IMPRINT",FACE,{"disambiguationData":[TD([[makeQuery(id+"F24.imprint","IMPRINT",EDGE,{"derivedFrom":sQuery(id+"F24.wireOp",EDGE,"E72.sketch_text.stroke-16")}),-1.0]])]});
            var Q2;
            Q2=makeQuery(id+"F24.imprint","IMPRINT",FACE,{"disambiguationData":[TD([[makeQuery(id+"F24.imprint","IMPRINT",EDGE,{"derivedFrom":sQuery(id+"F24.wireOp",EDGE,"E72.sketch_text.stroke-31")}),-1.0]])]});
            var Q3;
            Q3=makeQuery(id+"F24.imprint","IMPRINT",FACE,{"disambiguationData":[TD([[makeQuery(id+"F24.imprint","IMPRINT",EDGE,{"derivedFrom":sQuery(id+"F24.wireOp",EDGE,"E72.sketch_text.stroke-39")}),-1.0]])]});
            var Q4;
            Q4=makeQuery(id+"F24.imprint","IMPRINT",FACE,{"disambiguationData":[TD([[makeQuery(id+"F24.imprint","IMPRINT",EDGE,{"derivedFrom":sQuery(id+"F24.wireOp",EDGE,"E72.sketch_text.stroke-55")}),-1.0]])]});
            var Q5;
            Q5=makeQuery(id+"F24.imprint","IMPRINT",FACE,{"disambiguationData":[TD([[makeQuery(id+"F24.imprint","IMPRINT",EDGE,{"derivedFrom":sQuery(id+"F24.wireOp",EDGE,"E72.sketch_text.stroke-80")}),-1.0]])]});
            var Q6;
            Q6=makeQuery(id+"F24.imprint","IMPRINT",FACE,{"disambiguationData":[TD([[makeQuery(id+"F24.imprint","IMPRINT",EDGE,{"derivedFrom":sQuery(id+"F24.wireOp",EDGE,"E72.sketch_text.stroke-92")}),-1.0]])]});
            var Q7;
            Q7=makeQuery(id+"F24.imprint","IMPRINT",FACE,{"disambiguationData":[TD([[makeQuery(id+"F24.imprint","IMPRINT",EDGE,{"derivedFrom":sQuery(id+"F24.wireOp",EDGE,"E72.sketch_text.stroke-98")}),-1.0]])]});
            extrude(context, id + "F31", {"entities" : qUnion([Q0, Q1, Q2, Q3, Q4, Q5, Q6, Q7]), "operationType" : NewBodyOperationType.REMOVE, "oppositeDirection" : true, "depth" : 1.5 * mm});
        }
        {
            var Q0;
            Q0=makeQuery(id+"F22.imprint","IMPRINT",FACE,{"disambiguationData":[TD([[makeQuery(id+"F22.imprint","IMPRINT",EDGE,{"derivedFrom":sQuery(id+"F22.wireOp",EDGE,"E67.sketch_text.stroke-0")}),-1.0]])]});
            var Q1;
            Q1=makeQuery(id+"F22.imprint","IMPRINT",FACE,{"disambiguationData":[TD([[makeQuery(id+"F22.imprint","IMPRINT",EDGE,{"derivedFrom":sQuery(id+"F22.wireOp",EDGE,"E67.sketch_text.stroke-25")}),-1.0]])]});
            var Q2;
            Q2=makeQuery(id+"F22.imprint","IMPRINT",FACE,{"disambiguationData":[TD([[makeQuery(id+"F22.imprint","IMPRINT",EDGE,{"derivedFrom":sQuery(id+"F22.wireOp",EDGE,"E67.sketch_text.stroke-37")}),-1.0]])]});
            var Q3;
            Q3=makeQuery(id+"F22.imprint","IMPRINT",FACE,{"disambiguationData":[TD([[makeQuery(id+"F22.imprint","IMPRINT",EDGE,{"derivedFrom":sQuery(id+"F22.wireOp",EDGE,"E67.sketch_text.stroke-52")}),-1.0]])]});
            var Q4;
            Q4=makeQuery(id+"F22.imprint","IMPRINT",FACE,{"disambiguationData":[TD([[makeQuery(id+"F22.imprint","IMPRINT",EDGE,{"derivedFrom":sQuery(id+"F22.wireOp",EDGE,"E67.sketch_text.stroke-60")}),-1.0]])]});
            var Q5;
            Q5=makeQuery(id+"F22.imprint","IMPRINT",FACE,{"disambiguationData":[TD([[makeQuery(id+"F22.imprint","IMPRINT",EDGE,{"derivedFrom":sQuery(id+"F22.wireOp",EDGE,"E67.sketch_text.stroke-72")}),-1.0]])]});
            var Q6;
            Q6=makeQuery(id+"F22.imprint","IMPRINT",FACE,{"disambiguationData":[TD([[makeQuery(id+"F22.imprint","IMPRINT",EDGE,{"derivedFrom":sQuery(id+"F22.wireOp",EDGE,"E67.sketch_text.stroke-90")}),-1.0]])]});
            var Q7;
            Q7=makeQuery(id+"F22.imprint","IMPRINT",FACE,{"disambiguationData":[TD([[makeQuery(id+"F22.imprint","IMPRINT",EDGE,{"derivedFrom":sQuery(id+"F22.wireOp",EDGE,"E67.sketch_text.stroke-115")}),-1.0]])]});
            var Q8;
            Q8=makeQuery(id+"F22.imprint","IMPRINT",FACE,{"disambiguationData":[TD([[makeQuery(id+"F22.imprint","IMPRINT",EDGE,{"derivedFrom":sQuery(id+"F22.wireOp",EDGE,"E67.sketch_text.stroke-127")}),-1.0]])]});
            var Q9;
            Q9=makeQuery(id+"F22.imprint","IMPRINT",FACE,{"disambiguationData":[TD([[makeQuery(id+"F22.imprint","IMPRINT",EDGE,{"derivedFrom":sQuery(id+"F22.wireOp",EDGE,"E67.sketch_text.stroke-133")}),-1.0]])]});
            extrude(context, id + "F32", {"entities" : qUnion([Q0, Q1, Q2, Q3, Q4, Q5, Q6, Q7, Q8, Q9]), "operationType" : NewBodyOperationType.REMOVE, "oppositeDirection" : true, "depth" : 1.5 * mm});
        }
        {
            var Q0;
            Q0=makeQuery(id+"F20.imprint","IMPRINT",FACE,{"disambiguationData":[TD([[makeQuery(id+"F20.imprint","IMPRINT",EDGE,{"derivedFrom":sQuery(id+"F20.wireOp",EDGE,"E57.sketch_text.stroke-0")}),-1.0]])]});
            var Q1;
            Q1=makeQuery(id+"F20.imprint","IMPRINT",FACE,{"disambiguationData":[TD([[makeQuery(id+"F20.imprint","IMPRINT",EDGE,{"derivedFrom":sQuery(id+"F20.wireOp",EDGE,"E57.sketch_text.stroke-13")}),-1.0]])]});
            var Q2;
            Q2=makeQuery(id+"F20.imprint","IMPRINT",FACE,{"disambiguationData":[TD([[makeQuery(id+"F20.imprint","IMPRINT",EDGE,{"derivedFrom":sQuery(id+"F20.wireOp",EDGE,"E57.sketch_text.stroke-27")}),-1.0]])]});
            var Q3;
            Q3=makeQuery(id+"F20.imprint","IMPRINT",FACE,{"disambiguationData":[TD([[makeQuery(id+"F20.imprint","IMPRINT",EDGE,{"derivedFrom":sQuery(id+"F20.wireOp",EDGE,"E57.sketch_text.stroke-47")}),-1.0]])]});
            var Q4;
            Q4=makeQuery(id+"F20.imprint","IMPRINT",FACE,{"disambiguationData":[TD([[makeQuery(id+"F20.imprint","IMPRINT",EDGE,{"derivedFrom":sQuery(id+"F20.wireOp",EDGE,"E57.sketch_text.stroke-29")}),-1.0]])]});
            extrude(context, id + "F33", {"entities" : qUnion([Q0, Q1, Q2, Q3, Q4]), "operationType" : NewBodyOperationType.REMOVE, "oppositeDirection" : true, "depth" : 1.5 * mm});
        }
        {
            var Q0;
            Q0=makeQuery(id+"F18.imprint","IMPRINT",FACE,{"disambiguationData":[TD([[makeQuery(id+"F18.imprint","IMPRINT",EDGE,{"derivedFrom":sQuery(id+"F18.wireOp",EDGE,"E48.sketch_text.stroke-0")}),-1.0]])]});
            var Q1;
            Q1=makeQuery(id+"F18.imprint","IMPRINT",FACE,{"disambiguationData":[TD([[makeQuery(id+"F18.imprint","IMPRINT",EDGE,{"derivedFrom":sQuery(id+"F18.wireOp",EDGE,"E48.sketch_text.stroke-10")}),-1.0]])]});
            var Q2;
            Q2=makeQuery(id+"F18.imprint","IMPRINT",FACE,{"disambiguationData":[TD([[makeQuery(id+"F18.imprint","IMPRINT",EDGE,{"derivedFrom":sQuery(id+"F18.wireOp",EDGE,"E48.sketch_text.stroke-24")}),-1.0]])]});
            var Q3;
            Q3=makeQuery(id+"F18.imprint","IMPRINT",FACE,{"disambiguationData":[TD([[makeQuery(id+"F18.imprint","IMPRINT",EDGE,{"derivedFrom":sQuery(id+"F18.wireOp",EDGE,"E48.sketch_text.stroke-30")}),-1.0]])]});
            var Q4;
            Q4=makeQuery(id+"F18.imprint","IMPRINT",FACE,{"disambiguationData":[TD([[makeQuery(id+"F18.imprint","IMPRINT",EDGE,{"derivedFrom":sQuery(id+"F18.wireOp",EDGE,"E48.sketch_text.stroke-40")}),-1.0]])]});
            var Q5;
            Q5=makeQuery(id+"F18.imprint","IMPRINT",FACE,{"disambiguationData":[TD([[makeQuery(id+"F18.imprint","IMPRINT",EDGE,{"derivedFrom":sQuery(id+"F18.wireOp",EDGE,"E48.sketch_text.stroke-52")}),-1.0]])]});
            var Q6;
            Q6=makeQuery(id+"F18.imprint","IMPRINT",FACE,{"disambiguationData":[TD([[makeQuery(id+"F18.imprint","IMPRINT",EDGE,{"derivedFrom":sQuery(id+"F18.wireOp",EDGE,"E48.sketch_text.stroke-34")}),-1.0]])]});
            extrude(context, id + "F34", {"entities" : qUnion([Q0, Q1, Q2, Q3, Q4, Q5, Q6]), "operationType" : NewBodyOperationType.REMOVE, "oppositeDirection" : true, "depth" : 1.5 * mm});
        }
        {
            var Q0;
            Q0=makeQuery(id+"F16.imprint","IMPRINT",FACE,{"disambiguationData":[TD([[makeQuery(id+"F16.imprint","IMPRINT",EDGE,{"derivedFrom":sQuery(id+"F16.wireOp",EDGE,"E40.sketch_text.stroke-0")}),-1.0]])]});
            var Q1;
            Q1=makeQuery(id+"F16.imprint","IMPRINT",FACE,{"disambiguationData":[TD([[makeQuery(id+"F16.imprint","IMPRINT",EDGE,{"derivedFrom":sQuery(id+"F16.wireOp",EDGE,"E40.sketch_text.stroke-10")}),-1.0]])]});
            var Q2;
            Q2=makeQuery(id+"F16.imprint","IMPRINT",FACE,{"disambiguationData":[TD([[makeQuery(id+"F16.imprint","IMPRINT",EDGE,{"derivedFrom":sQuery(id+"F16.wireOp",EDGE,"E40.sketch_text.stroke-24")}),-1.0]])]});
            var Q3;
            Q3=makeQuery(id+"F16.imprint","IMPRINT",FACE,{"disambiguationData":[TD([[makeQuery(id+"F16.imprint","IMPRINT",EDGE,{"derivedFrom":sQuery(id+"F16.wireOp",EDGE,"E40.sketch_text.stroke-39")}),-1.0]])]});
            extrude(context, id + "F35", {"entities" : qUnion([Q0, Q1, Q2, Q3]), "operationType" : NewBodyOperationType.REMOVE, "oppositeDirection" : true, "depth" : 1.5 * mm});
        }
        {
            var Q0;
            Q0=makeQuery(id+"F14.imprint","IMPRINT",FACE,{"disambiguationData":[TD([[makeQuery(id+"F14.imprint","IMPRINT",EDGE,{"derivedFrom":sQuery(id+"F14.wireOp",EDGE,"E33.sketch_text.stroke-0")}),-1.0]])]});
            var Q1;
            Q1=makeQuery(id+"F14.imprint","IMPRINT",FACE,{"disambiguationData":[TD([[makeQuery(id+"F14.imprint","IMPRINT",EDGE,{"derivedFrom":sQuery(id+"F14.wireOp",EDGE,"E33.sketch_text.stroke-18")}),-1.0]])]});
            var Q2;
            Q2=makeQuery(id+"F14.imprint","IMPRINT",FACE,{"disambiguationData":[TD([[makeQuery(id+"F14.imprint","IMPRINT",EDGE,{"derivedFrom":sQuery(id+"F14.wireOp",EDGE,"E33.sketch_text.stroke-31")}),-1.0]])]});
            extrude(context, id + "F36", {"entities" : qUnion([Q0, Q1, Q2]), "operationType" : NewBodyOperationType.REMOVE, "oppositeDirection" : true, "depth" : 1.5 * mm});
        }
    });
